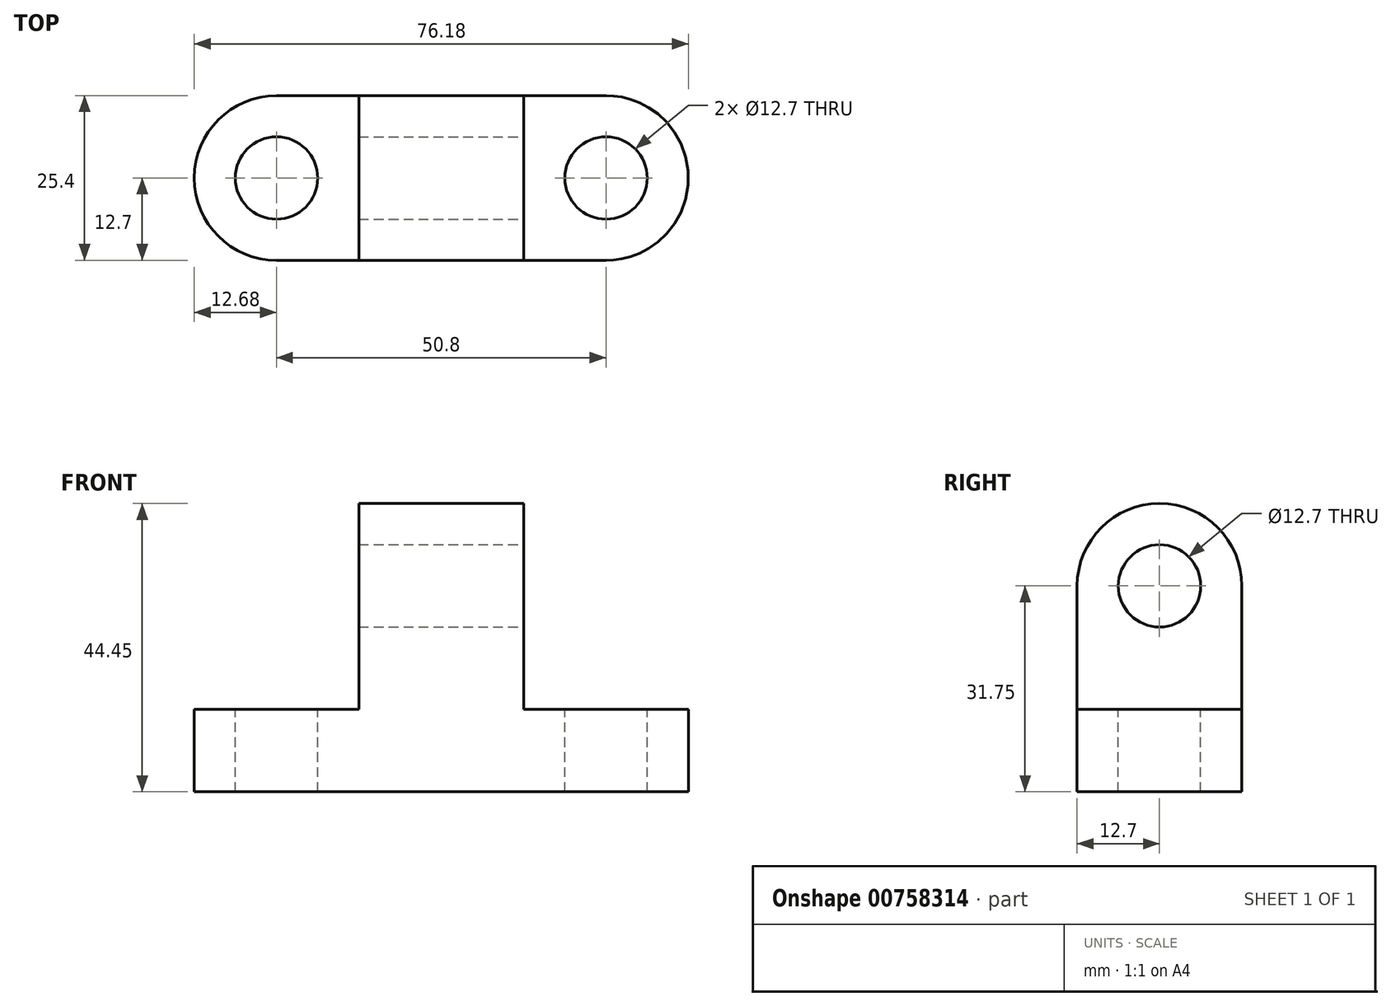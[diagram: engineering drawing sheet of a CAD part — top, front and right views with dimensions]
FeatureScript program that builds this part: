
annotation { "Feature Type Name" : "Feature", "Feature Type Description" : "" }
export const myFeature = defineFeature(function(context is Context, id is Id, definition is map)
    precondition{}
    {
        {
            var Q0;
            Q0=qCreatedBy(makeId("Front.planeOp"),FACE);
            var sketch = newSketch(context, id + "F0", { "sketchPlane" : qUnion([Q0])});
            skLineSegment(sketch, "E0", {"start": v(0, 0) * mm, "end": v(0, 12.7) * mm});
            skLineSegment(sketch, "E1", {"start": v(0, 12.7) * mm, "end": v(25.4, 12.7) * mm});
            skLineSegment(sketch, "E2", {"start": v(25.4, 12.7) * mm, "end": v(25.4, 44.45) * mm});
            skLineSegment(sketch, "E3", {"start": v(25.4, 44.45) * mm, "end": v(50.8, 44.45) * mm});
            skLineSegment(sketch, "E4", {"start": v(50.8, 44.45) * mm, "end": v(50.8, 12.7) * mm});
            skLineSegment(sketch, "E5", {"start": v(50.8, 12.7) * mm, "end": v(76.2, 12.7) * mm});
            skLineSegment(sketch, "E6", {"start": v(76.2, 12.7) * mm, "end": v(76.2, 0) * mm});
            skLineSegment(sketch, "E7", {"start": v(76.2, 0) * mm, "end": v(0, 0) * mm});
            skSolve(sketch);
        }
        {
            var Q0;
            Q0=makeQuery(id+"F0.imprint","IMPRINT",FACE,{"disambiguationData":[TD([[makeQuery(id+"F0.imprint","IMPRINT",EDGE,{"derivedFrom":sQuery(id+"F0.wireOp",EDGE,"E0")}),-1.0]])]});
            extrude(context, id + "F1", {"entities" : qUnion([Q0]), "depth" : 25.4 * mm, "offsetDistance" : 25.4 * mm});
        }
        {
            var Q0;
            Q0=makeQuery(id+"F1.opExtrude","SWEPT_FACE",FACE,{"disambiguationData":[OSD([sQuery(id+"F0.wireOp",EDGE,"E4")])]});
            var sketch = newSketch(context, id + "F2", { "sketchPlane" : qUnion([Q0])});
            skCircle(sketch, "E8", {"center": v(-12.7, 31.75) * mm, "radius": 6.35 * mm});
            skArc(sketch, "E9", {"start": v(0, 31.75) * mm, "mid": v(-12.7, 44.45) * mm, "end": v(-25.4, 31.75) * mm});
            skSolve(sketch);
        }
        {
            var Q0;
            {var subQ0=sQuery(id+"F2.wireOp",EDGE,"E9");var subQ1=sQuery(id+"F0.wireOp",EDGE,"E4");var subQ2=makeQuery(id+"F1.opExtrude","CAP_EDGE",EDGE,{"disambiguationData":[OSD([subQ1])],"isStart":false});var subQ3=makeQuery(id+"F2.imprint","INTERSECT",VERTEX,{"derivedFrom":[subQ2,subQ0]});Q0=makeQuery(id+"F2.imprint","IMPRINT",FACE,{"disambiguationData":[TD([[makeQuery(id+"F2.imprint","IMPRINT",EDGE,{"disambiguationData":[TD([[subQ3,1.0]])],"derivedFrom":subQ0}),-1.0]])]});}
            var Q1;
            {var subQ0=sQuery(id+"F2.wireOp",EDGE,"E9");var subQ1=sQuery(id+"F0.wireOp",EDGE,"E4");var subQ2=makeQuery(id+"F1.opExtrude","CAP_EDGE",EDGE,{"disambiguationData":[OSD([subQ1])],"isStart":true});var subQ3=makeQuery(id+"F2.imprint","INTERSECT",VERTEX,{"derivedFrom":[subQ2,subQ0]});Q1=makeQuery(id+"F2.imprint","IMPRINT",FACE,{"disambiguationData":[TD([[makeQuery(id+"F2.imprint","IMPRINT",EDGE,{"disambiguationData":[TD([[subQ3,-1.0]])],"derivedFrom":subQ0}),-1.0]])]});}
            var Q2;
            Q2=makeQuery(id+"F2.imprint","IMPRINT",FACE,{"disambiguationData":[TD([[makeQuery(id+"F2.imprint","IMPRINT",EDGE,{"derivedFrom":sQuery(id+"F2.wireOp",EDGE,"E8")}),1.0]])]});
            extrude(context, id + "F3", {"entities" : qUnion([Q0, Q1, Q2]), "operationType" : NewBodyOperationType.REMOVE, "oppositeDirection" : true, "depth" : 25.4 * mm, "offsetDistance" : 25.4 * mm});
        }
        {
            var Q0;
            Q0=makeQuery(id+"F1.opExtrude","SWEPT_FACE",FACE,{"disambiguationData":[OSD([sQuery(id+"F0.wireOp",EDGE,"E1")])]});
            var sketch = newSketch(context, id + "F4", { "sketchPlane" : qUnion([Q0])});
            skCircle(sketch, "E10", {"center": v(12.7, -12.7) * mm, "radius": 6.35 * mm});
            skArc(sketch, "E11", {"start": v(12.7, 0) * mm, "mid": v(0.02, -12.7) * mm, "end": v(12.7, -25.4) * mm});
            skArc(sketch, "E12", {"start": v(63.5, -25.4) * mm, "mid": v(76.2, -12.7) * mm, "end": v(63.5, 0) * mm});
            skCircle(sketch, "E13", {"center": v(63.5, -12.7) * mm, "radius": 6.35 * mm});
            skLineSegment(sketch, "E14", {"start": v(63.5, -25.4) * mm, "end": v(94.46, -25.4) * mm});
            skLineSegment(sketch, "E15", {"start": v(94.46, -25.4) * mm, "end": v(94.46, 0) * mm});
            skLineSegment(sketch, "E16", {"start": v(94.46, 0) * mm, "end": v(63.5, 0) * mm});
            skSolve(sketch);
        }
        {
            var Q0;
            Q0=makeQuery(id+"F4.imprint","IMPRINT",FACE,{"disambiguationData":[TD([[makeQuery(id+"F4.imprint","IMPRINT",EDGE,{"derivedFrom":sQuery(id+"F4.wireOp",EDGE,"E13")}),1.0]])]});
            var Q1;
            Q1=makeQuery(id+"F4.imprint","IMPRINT",FACE,{"disambiguationData":[TD([[makeQuery(id+"F4.imprint","IMPRINT",EDGE,{"derivedFrom":sQuery(id+"F4.wireOp",EDGE,"E10")}),1.0]])]});
            var Q2;
            Q2=makeQuery(id+"F4.imprint","IMPRINT",FACE,{"disambiguationData":[TD([[makeQuery(id+"F4.imprint","IMPRINT",EDGE,{"derivedFrom":sQuery(id+"F4.wireOp",EDGE,"E12")}),-1.0]])]});
            var Q3;
            {var subQ0=sQuery(id+"F4.wireOp",EDGE,"E11");Q3=makeQuery(id+"F4.imprint","IMPRINT",FACE,{"disambiguationData":[TD([[makeQuery(id+"F4.imprint","IMPRINT",EDGE,{"derivedFrom":subQ0}),-1.0]])]});}
            extrude(context, id + "F5", {"entities" : qUnion([Q0, Q1, Q2, Q3]), "operationType" : NewBodyOperationType.REMOVE, "oppositeDirection" : true, "depth" : 25.4 * mm, "offsetDistance" : 25.4 * mm});
        }
    });
